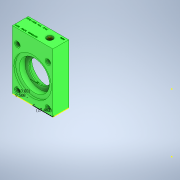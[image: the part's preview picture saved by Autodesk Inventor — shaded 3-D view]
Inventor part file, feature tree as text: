
AUTODESK INVENTOR PART (.ipt)
format: ipt  version: 2020 (Build 240168000, 168)  size: 565,760 bytes
history: native  units: in
note: dims shown in document units (in); Inventor stores cm internally (conversion verified against a paired STEP export)
features: sketch x6, hole x4, extrude x3, imported_body x1
ambient origin geometry x8: Origin, YZ Plane, XZ Plane, XY Plane, X Axis, Y Axis, Z Axis, Center Point
bodies: Solid1 (feature_tree)
feature tree (14):
  extrude  "Extrusion1"  Depth=0.3937in TaperAngle=0.0deg
  extrude  "Extrusion2"  Depth=0.375in
  sketch  "Sketch3"  dims[d11=0.213in d12=0.2362in d13=0.4375in d14=0.25in d15=0.563in d16=0.375in d17=0.0in d18=0.3743in]
  hole  "Hole1"  [1 undecoded]
  hole  "Hole2"  [1 undecoded]
  sketch  "Sketch6"  dims[d36=0.6875in]
  extrude  "Extrusion3"  [1 undecoded]
  hole  "Hole5"  [1 undecoded]
  hole  "Hole6"  [1 undecoded]
  sketch  "Sketch1"  dims[d0=0.6398in d1=0.0in d2=0.3937in d3=0.0in]
  sketch  "Sketch2"  dims[d4=0.04in d5=0.2362in d6=0.4375in d7=0.25in d8=0.563in d9=0.9843in d10=0.8108in]
  sketch  "Sketch5"  dims[d19=0.0in d34=0.1181in d35=0.0in]
  sketch  "Sketch8"  dims[d37=0.213in d38=0.2362in d39=0.1575in d40=0.0787in d41=90.0deg d42=0.25in d43=0.0in d44=0.04in d45=0.2362in d46=0.1575in d47=0.0787in d48=90.0deg d49=0.4724in d50=0.481in d51=0.2701in]
  imported_body  "Base1"
note: 5 required parameter values undecoded (feature->parameter linkage not recoverable at this tier; creation-order binding heuristic only, values carry confidence <= 0.55)
